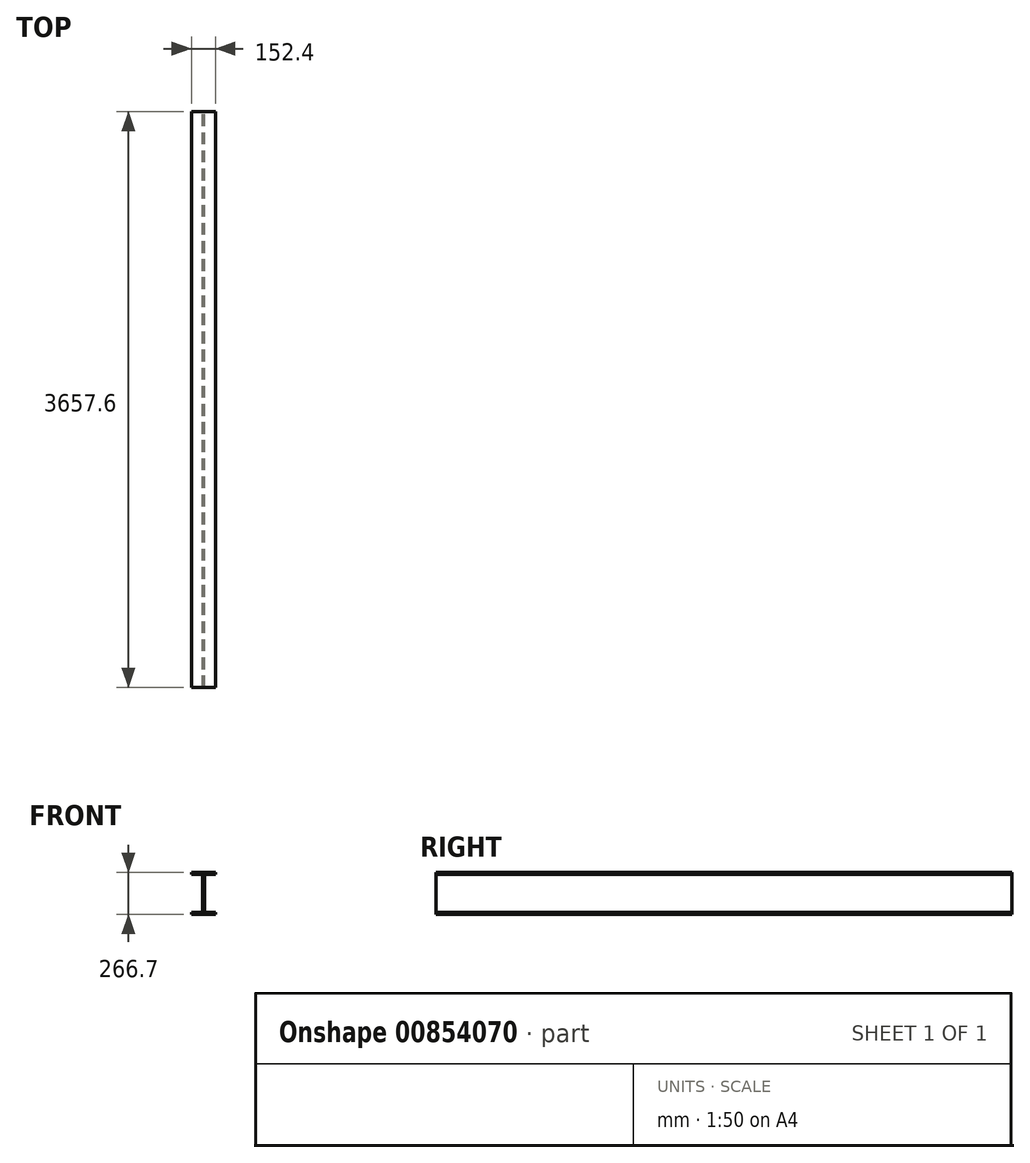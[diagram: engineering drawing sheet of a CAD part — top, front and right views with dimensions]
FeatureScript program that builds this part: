
annotation { "Feature Type Name" : "Feature", "Feature Type Description" : "" }
export const myFeature = defineFeature(function(context is Context, id is Id, definition is map)
    precondition{}
    {
        {
            var Q0;
            Q0=qCreatedBy(makeId("Front.planeOp"),FACE);
            var sketch = newSketch(context, id + "F0", { "sketchPlane" : qUnion([Q0])});
            skLineSegment(sketch, "E0.bottom", {"start": v(6.35, 127) * mm, "end": v(-6.35, 127) * mm});
            skLineSegment(sketch, "E0.top", {"start": v(6.35, -127) * mm, "end": v(-6.35, -127) * mm});
            skLineSegment(sketch, "E0.left", {"start": v(6.35, 127) * mm, "end": v(6.35, -127) * mm});
            skLineSegment(sketch, "E0.right", {"start": v(-6.35, 127) * mm, "end": v(-6.35, -127) * mm});
            skPoint(sketch, "E0.middle", {"position": v(0, 0) * mm});
            skLineSegment(sketch, "E1.bottom", {"start": v(76.2, 120.65) * mm, "end": v(-76.2, 120.65) * mm});
            skLineSegment(sketch, "E1.top", {"start": v(76.2, 133.35) * mm, "end": v(-76.2, 133.35) * mm});
            skLineSegment(sketch, "E1.left", {"start": v(76.2, 120.65) * mm, "end": v(76.2, 133.35) * mm});
            skLineSegment(sketch, "E1.right", {"start": v(-76.2, 120.65) * mm, "end": v(-76.2, 133.35) * mm});
            skPoint(sketch, "E1.middle", {"position": v(0, 127) * mm});
            skLineSegment(sketch, "E2.bottom", {"start": v(76.2, -133.35) * mm, "end": v(-76.2, -133.35) * mm});
            skLineSegment(sketch, "E2.top", {"start": v(76.2, -120.65) * mm, "end": v(-76.2, -120.65) * mm});
            skLineSegment(sketch, "E2.left", {"start": v(76.2, -133.35) * mm, "end": v(76.2, -120.65) * mm});
            skLineSegment(sketch, "E2.right", {"start": v(-76.2, -133.35) * mm, "end": v(-76.2, -120.65) * mm});
            skPoint(sketch, "E2.middle", {"position": v(0, -127) * mm});
            skSolve(sketch);
        }
        {
            var Q0;
            Q0 = qSketchRegion(id + "F0", true);
            extrude(context, id + "F1", {"entities" : qUnion([Q0]), "endBound" : BoundingType.SYMMETRIC, "depth" : 3657.6 * mm, "offsetDistance" : 25.4 * mm});
        }
    });
